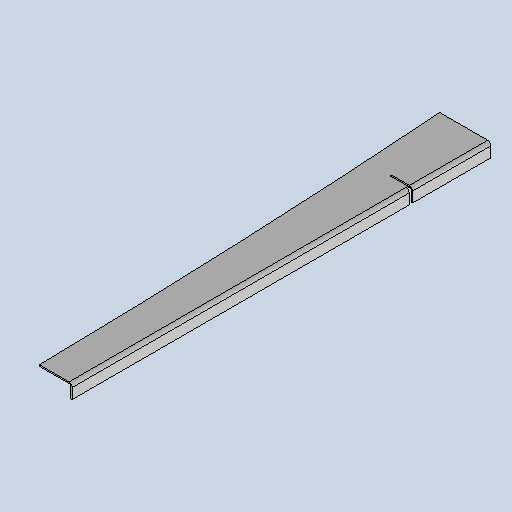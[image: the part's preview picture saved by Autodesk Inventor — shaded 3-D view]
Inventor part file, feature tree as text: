
AUTODESK INVENTOR PART (.ipt)
format: ipt  version: 2025 (Build 290162010, 162A)  size: 451,072 bytes
history: native  units: mm
features: sketch x6, other x5, sheet_metal_op x4, projected_geometry x4, extrude x2, chamfer x1, pattern_linear x1
ambient origin geometry x8: Origin, YZ Plane, XZ Plane, XY Plane, X Axis, Y Axis, Z Axis, Center Point
bodies: Body1 (feature_tree)
feature tree (23):
  sheet_metal_op  "Face2"
  sheet_metal_op  "Flange2"
  extrude  "Extrusion2"  Depth=6.0mm
  chamfer  "Chamfer2"  Distance=2.75mm
  pattern_linear  "Rectangular Pattern3"  Count1=2 Spacing1=90.0deg
  other  "Mark1"
  other  "A-Side Definition"
  extrude  "Extrusion3"  Depth=2.0mm
  sketch  "Sketch1"  dims[d16=1500.0mm d17=2700.0mm d18=2100.0mm d19=6.0mm d20=3.0mm d21=3.0mm d22=6.0mm d23=3.0mm d24=241.9mm d25=50.0mm d26=50.0mm d27=3.0mm d28=110.0mm d29=25.0mm d30=104.0mm d31=25.0mm d32=20.0mm d33=50.0mm d37=6.0mm d38=3.0mm d39=3.0mm]
  other  "Plate3"
  sketch  "Sketch3"  dims[d46=2.0mm]
  other  "Plate4"
  sheet_metal_op  "Bend2"
  sheet_metal_op  "Corner2"
  sketch  "Sketch5"  dims[d47=2.0mm]
  projected_geometry  "Projected Loop2"
  sketch  "Sketch Rectangular Pattern1"  dims[d43=3.0mm]
  sketch  "Sketch6"  dims[d48=1.0mm]
  sketch  "Sketch7"  dims[d49=4.0mm d50=2.75mm d51=20.0mm d52=90.0deg d53=2.75mm d54=8.0mm d55=2.0mm d56=2.75mm d57=500.0mm d58=500.0mm d59=500.0mm d60=500.0mm d61=500.0mm d69=1839.242466mm d70=2.0mm d71=0.0mm d72=0.0mm d76=67.563014mm d77=30.0mm d79=30.0mm d80=48.359031mm d81=30.0mm d83=250.0mm d84=40.0mm d86=550.0mm d87=10.0mm d89=10.0mm d91=274.556536mm d94=5.0mm d95=30.0mm d96=5.0mm d97=30.0mm d98=5.0mm d102=77.905549mm d104=51.799453mm d106=2.0mm d107=5.0mm d108=116.0mm d109=500.0mm d110=500.0mm d111=500.0mm d112=31.0mm d113=40.0mm d115=500.0mm d117=8.0mm d118=2.0mm d119=45.0deg d120=200.0mm d121=14.0mm d124=50.0mm d125=12.0mm d126=50.0mm d127=25.0mm d128=50.0mm d129=12.0mm d130=50.0mm d131=12.0mm d132=50.0mm d133=12.0mm d134=50.0mm d135=25.0mm d136=25.0mm d137=25.0mm d138=50.0mm d139=50.0mm d140=50.0mm d141=0.0mm d142=0.0mm d143=80.0mm]
  projected_geometry  "Projected Loop3"
  projected_geometry  "Projected Loop4"
  projected_geometry  "Projected Loop5"
  other  "Definition1"
